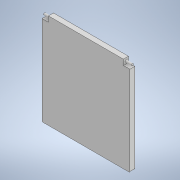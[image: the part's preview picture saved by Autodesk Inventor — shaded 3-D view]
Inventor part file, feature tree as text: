
AUTODESK INVENTOR PART (.ipt)
format: ipt  version: 2021 (Build 250183000, 183)  size: 126,976 bytes
history: native  units: mm
features: extrude x3, sketch x3, other x1
ambient origin geometry x8: Origin, YZ Plane, XZ Plane, XY Plane, X Axis, Y Axis, Z Axis, Center Point
bodies: Body1 (feature_tree)
feature tree (7):
  other  "Sólido1"
  extrude  "Extrusión1"  Depth=32.0mm
  extrude  "Extrusión2"  Depth=32.0mm
  extrude  "Extrusión3"  Depth=10.0mm
  sketch  "Boceto1"  dims[d0=435.0mm d2=32.0mm]
  sketch  "Boceto2"  dims[d3=27.0mm d4=32.0mm]
  sketch  "Boceto3"  dims[d5=25.0mm d6=0.0mm d7=10.0mm d8=32.0mm d9=403.0mm d10=0.0mm d11=0.0mm d14=48.0mm d15=25.0mm d16=15.0mm d17=0.0mm d18=5.0mm]
